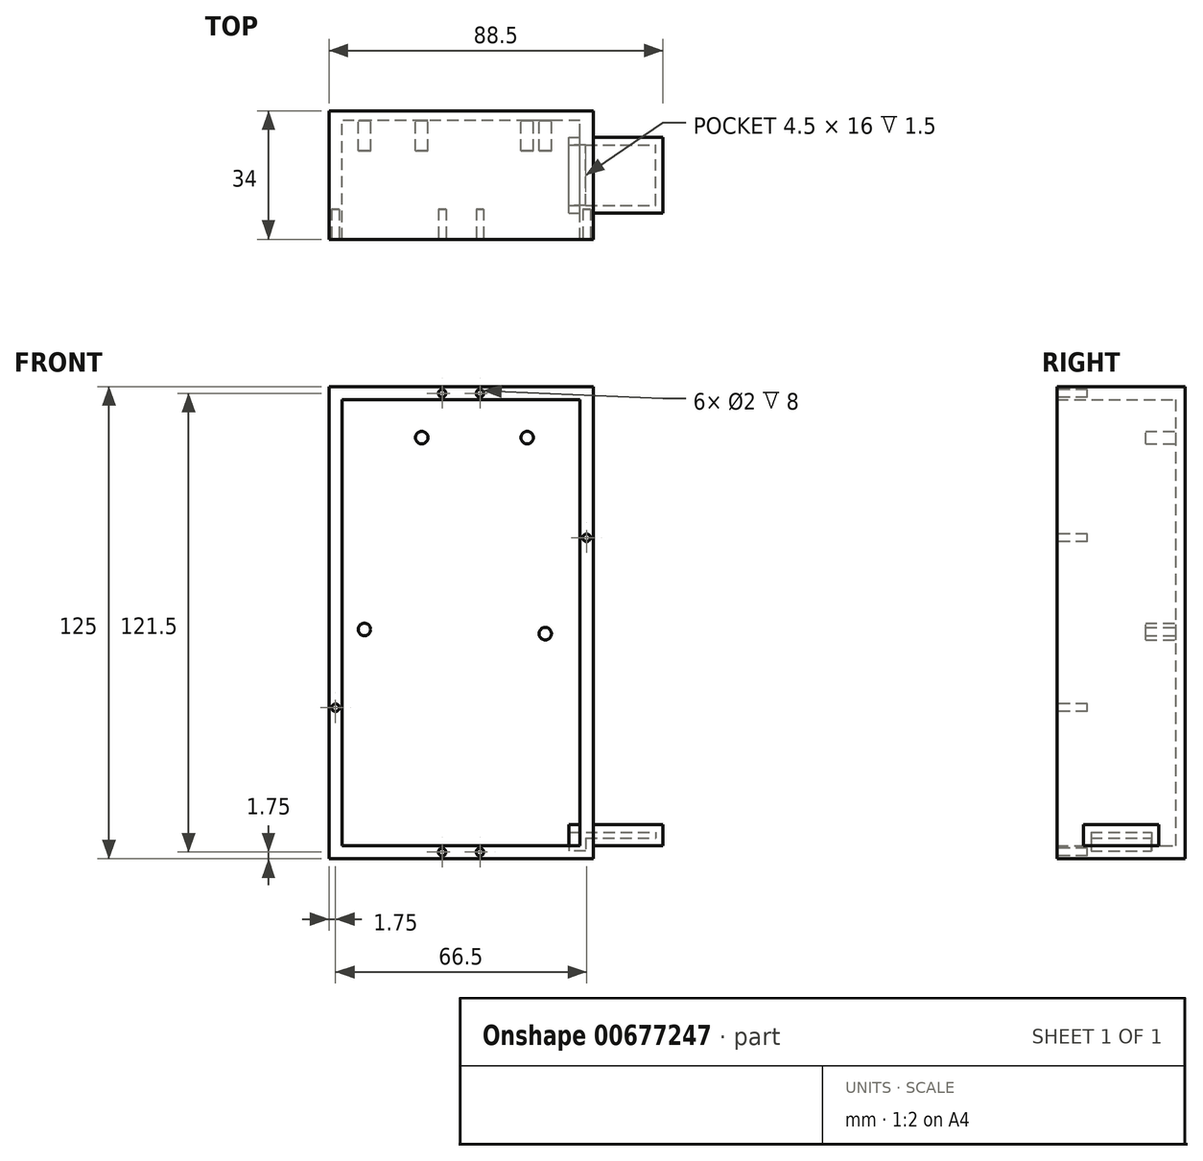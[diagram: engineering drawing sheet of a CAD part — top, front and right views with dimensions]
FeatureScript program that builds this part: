
annotation { "Feature Type Name" : "Feature", "Feature Type Description" : "" }
export const myFeature = defineFeature(function(context is Context, id is Id, definition is map)
    precondition{}
    {
        {
            var Q0;
            Q0=qCreatedBy(makeId("Front.planeOp"),FACE);
            var sketch = newSketch(context, id + "F0", { "sketchPlane" : qUnion([Q0])});
            skLineSegment(sketch, "E0.bottom", {"start": v(0, 0) * mm, "end": v(-70, 0) * mm});
            skLineSegment(sketch, "E0.top", {"start": v(0, 125) * mm, "end": v(-70, 125) * mm});
            skLineSegment(sketch, "E0.left", {"start": v(0, 0) * mm, "end": v(0, 125) * mm});
            skLineSegment(sketch, "E0.right", {"start": v(-70, 0) * mm, "end": v(-70, 125) * mm});
            skSolve(sketch);
        }
        {
            var Q0;
            Q0=qSketchRegion(id+"F0",true);
            extrude(context, id + "F1", {"entities" : qUnion([Q0]), "depth" : 35 * mm, "offsetDistance" : 25 * mm});
        }
        {
            var Q0;
            Q0=makeQuery(id+"F1.opExtrude","CAP_FACE",FACE,{"disambiguationData":[OSD([sQuery(id+"F0.wireOp",EDGE,"E0.bottom"),sQuery(id+"F0.wireOp",EDGE,"E0.top"),sQuery(id+"F0.wireOp",EDGE,"E0.left"),sQuery(id+"F0.wireOp",EDGE,"E0.right")])],"isStart":false});
            shell(context, id + "F2", {"entities" : qUnion([Q0]), "thickness" : 3.5 * mm});
        }
        {
            var Q0;
            Q0=makeQuery(id+"F2.opShell","OFFSET_FACE",FACE,{"disambiguationData":[OSD([sQuery(id+"F0.wireOp",EDGE,"E0.bottom"),sQuery(id+"F0.wireOp",EDGE,"E0.top"),sQuery(id+"F0.wireOp",EDGE,"E0.left"),sQuery(id+"F0.wireOp",EDGE,"E0.right")])]});
            var sketch = newSketch(context, id + "F3", { "sketchPlane" : qUnion([Q0])});
            skCircle(sketch, "E1", {"center": v(-45.4, 111.5) * mm, "radius": 1.65 * mm});
            skCircle(sketch, "E2", {"center": v(-17.5, 111.5) * mm, "radius": 1.65 * mm});
            skCircle(sketch, "E3", {"center": v(-12.7, 59.6) * mm, "radius": 1.65 * mm});
            skCircle(sketch, "E4", {"center": v(-60.6, 60.7) * mm, "radius": 1.65 * mm});
            skSolve(sketch);
        }
        {
            var Q0;
            Q0=qSketchRegion(id+"F3",true);
            extrude(context, id + "F4", {"entities" : qUnion([Q0]), "operationType" : NewBodyOperationType.ADD, "depth" : 8 * mm, "offsetDistance" : 25 * mm});
        }
        {
            var Q0;
            Q0=makeQuery(id+"F2.opShell","OFFSET_FACE",FACE,{"disambiguationData":[OSD([sQuery(id+"F0.wireOp",EDGE,"E0.bottom")])]});
            var sketch = newSketch(context, id + "F5", { "sketchPlane" : qUnion([Q0])});
            skLineSegment(sketch, "E5.bottom", {"start": v(-6.5, -28) * mm, "end": v(18.5, -28) * mm});
            skLineSegment(sketch, "E5.top", {"start": v(-6.5, -8) * mm, "end": v(18.5, -8) * mm});
            skLineSegment(sketch, "E5.left", {"start": v(-6.5, -28) * mm, "end": v(-6.5, -8) * mm});
            skLineSegment(sketch, "E5.right", {"start": v(18.5, -28) * mm, "end": v(18.5, -8) * mm});
            skSolve(sketch);
        }
        {
            var Q0;
            Q0=qSketchRegion(id+"F5",true);
            extrude(context, id + "F6", {"entities" : qUnion([Q0]), "operationType" : NewBodyOperationType.ADD, "depth" : 5.5 * mm, "offsetDistance" : 25 * mm});
        }
        {
            var Q0;
            Q0=makeQuery(id+"F6.opExtrude","SWEPT_FACE",FACE,{"disambiguationData":[OSD([sQuery(id+"F5.wireOp",EDGE,"E5.left")])]});
            shell(context, id + "F7", {"entities" : qUnion([Q0]), "thickness" : 2 * mm});
        }
        {
            var Q0;
            Q0=makeQuery(id+"F1.opExtrude","CAP_FACE",FACE,{"disambiguationData":[OSD([sQuery(id+"F0.wireOp",EDGE,"E0.bottom"),sQuery(id+"F0.wireOp",EDGE,"E0.top"),sQuery(id+"F0.wireOp",EDGE,"E0.left"),sQuery(id+"F0.wireOp",EDGE,"E0.right")])],"isStart":false});
            var sketch = newSketch(context, id + "F8", { "sketchPlane" : qUnion([Q0])});
            skCircle(sketch, "E6", {"center": v(-30, 123.25) * mm, "radius": 1 * mm});
            skCircle(sketch, "E7", {"center": v(-1.75, 85) * mm, "radius": 1 * mm});
            skCircle(sketch, "E8", {"center": v(-30, 1.75) * mm, "radius": 1 * mm});
            skCircle(sketch, "E9", {"center": v(-40, 1.75) * mm, "radius": 1 * mm});
            skCircle(sketch, "E10", {"center": v(-68.25, 40) * mm, "radius": 1 * mm});
            skCircle(sketch, "E11", {"center": v(-40, 123.25) * mm, "radius": 1 * mm});
            skSolve(sketch);
        }
        {
            var Q0;
            Q0=qSketchRegion(id+"F8",true);
            extrude(context, id + "F9", {"entities" : qUnion([Q0]), "operationType" : NewBodyOperationType.REMOVE, "oppositeDirection" : true, "depth" : 8 * mm, "offsetDistance" : 25 * mm});
        }
        {
            var Q0;
            Q0=makeQuery(id+"F1.opExtrude","CAP_FACE",FACE,{"disambiguationData":[OSD([sQuery(id+"F0.wireOp",EDGE,"E0.bottom"),sQuery(id+"F0.wireOp",EDGE,"E0.top"),sQuery(id+"F0.wireOp",EDGE,"E0.left"),sQuery(id+"F0.wireOp",EDGE,"E0.right")])],"isStart":true});
            var sketch = newSketch(context, id + "F10", { "sketchPlane" : qUnion([Q0])});
            skLineSegment(sketch, "E12.bottom", {"start": v(70, 125) * mm, "end": v(0, 125) * mm});
            skLineSegment(sketch, "E12.top", {"start": v(70, 0) * mm, "end": v(0, 0) * mm});
            skLineSegment(sketch, "E12.left", {"start": v(70, 125) * mm, "end": v(70, 0) * mm});
            skLineSegment(sketch, "E12.right", {"start": v(0, 125) * mm, "end": v(0, 0) * mm});
            skSolve(sketch);
        }
        {
            var Q0;
            Q0=qSketchRegion(id+"F10",true);
            extrude(context, id + "F11", {"entities" : qUnion([Q0]), "operationType" : NewBodyOperationType.REMOVE, "oppositeDirection" : true, "depth" : 1 * mm, "offsetDistance" : 25 * mm});
        }
    });
